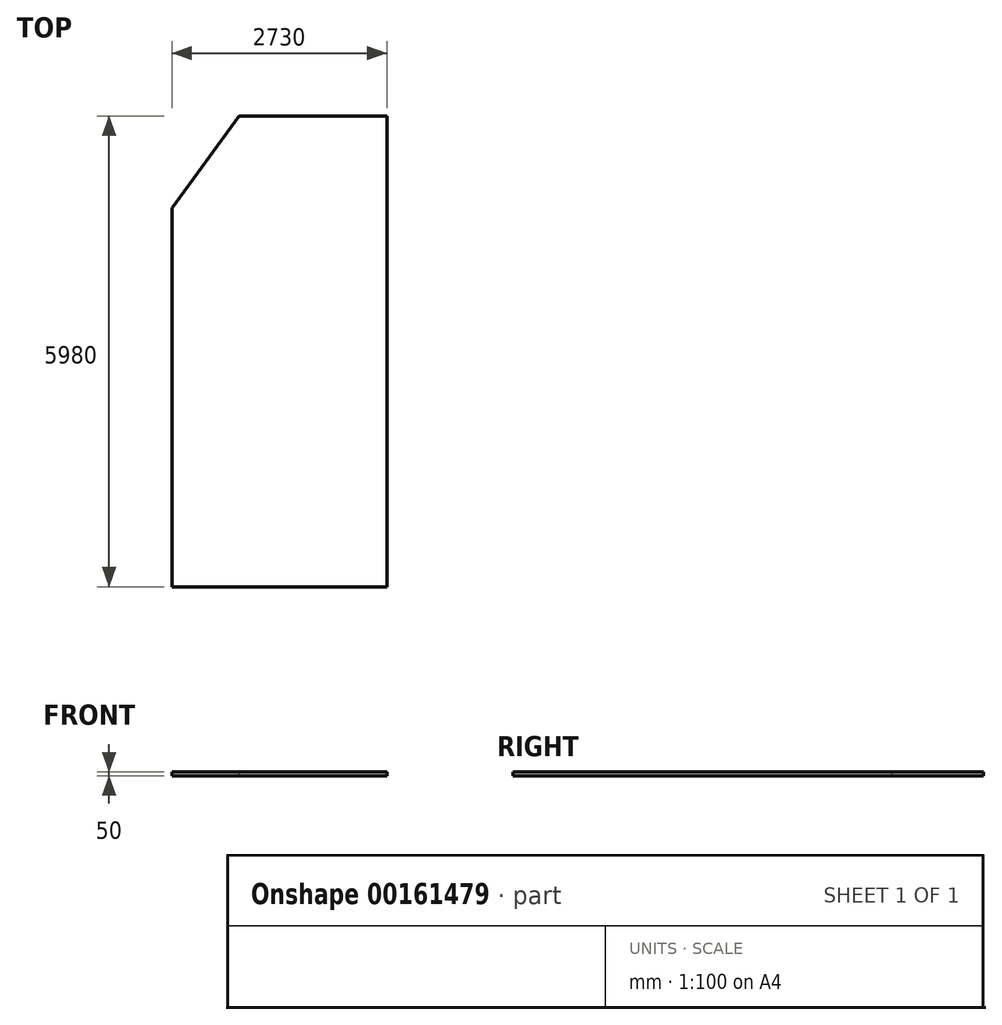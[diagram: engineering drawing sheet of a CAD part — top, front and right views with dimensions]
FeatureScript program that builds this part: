
annotation { "Feature Type Name" : "Feature", "Feature Type Description" : "" }
export const myFeature = defineFeature(function(context is Context, id is Id, definition is map)
    precondition{}
    {
        {
            var Q0;
            Q0=qCreatedBy(makeId("Top.planeOp"),FACE);
            var sketch = newSketch(context, id + "F0", { "sketchPlane" : qUnion([Q0])});
            skLineSegment(sketch, "E0.bottom", {"start": v(1365, 2990) * mm, "end": v(-515, 2990) * mm});
            skLineSegment(sketch, "E0.top", {"start": v(1365, -2990) * mm, "end": v(-1365, -2990) * mm});
            skLineSegment(sketch, "E0.left", {"start": v(1365, 2990) * mm, "end": v(1365, -2990) * mm});
            skLineSegment(sketch, "E0.right", {"start": v(-1365, 1820) * mm, "end": v(-1365, -2990) * mm});
            skPoint(sketch, "E0.middle", {"position": v(0, 0) * mm});
            skLineSegment(sketch, "E1", {"start": v(-515, 2990) * mm, "end": v(-1365, 1820) * mm});
            skPoint(sketch, "E2.orphan", {"position": v(-1365, 2990) * mm});
            skLineSegment(sketch, "E3", {"start": v(1365, -130) * mm, "end": v(-1365, -130) * mm, "construction": true});
            skSolve(sketch);
        }
        {
            var Q0;
            Q0 = qSketchRegion(id + "F0", true);
            extrude(context, id + "F1", {"entities" : qUnion([Q0]), "endBound" : BoundingType.SYMMETRIC, "depth" : 50 * mm});
        }
        {
            var Q0;
            Q0=makeQuery(id+"F1.opExtrude","SWEPT_FACE",FACE,{"disambiguationData":[OSD([sQuery(id+"F0.wireOp",EDGE,"E0.left")])]});
            var sketch = newSketch(context, id + "F2", { "sketchPlane" : qUnion([Q0])});
            skLineSegment(sketch, "E4", {"start": v(-130, 25) * mm, "end": v(-130, 0) * mm, "construction": true});
            skSolve(sketch);
        }
    });
